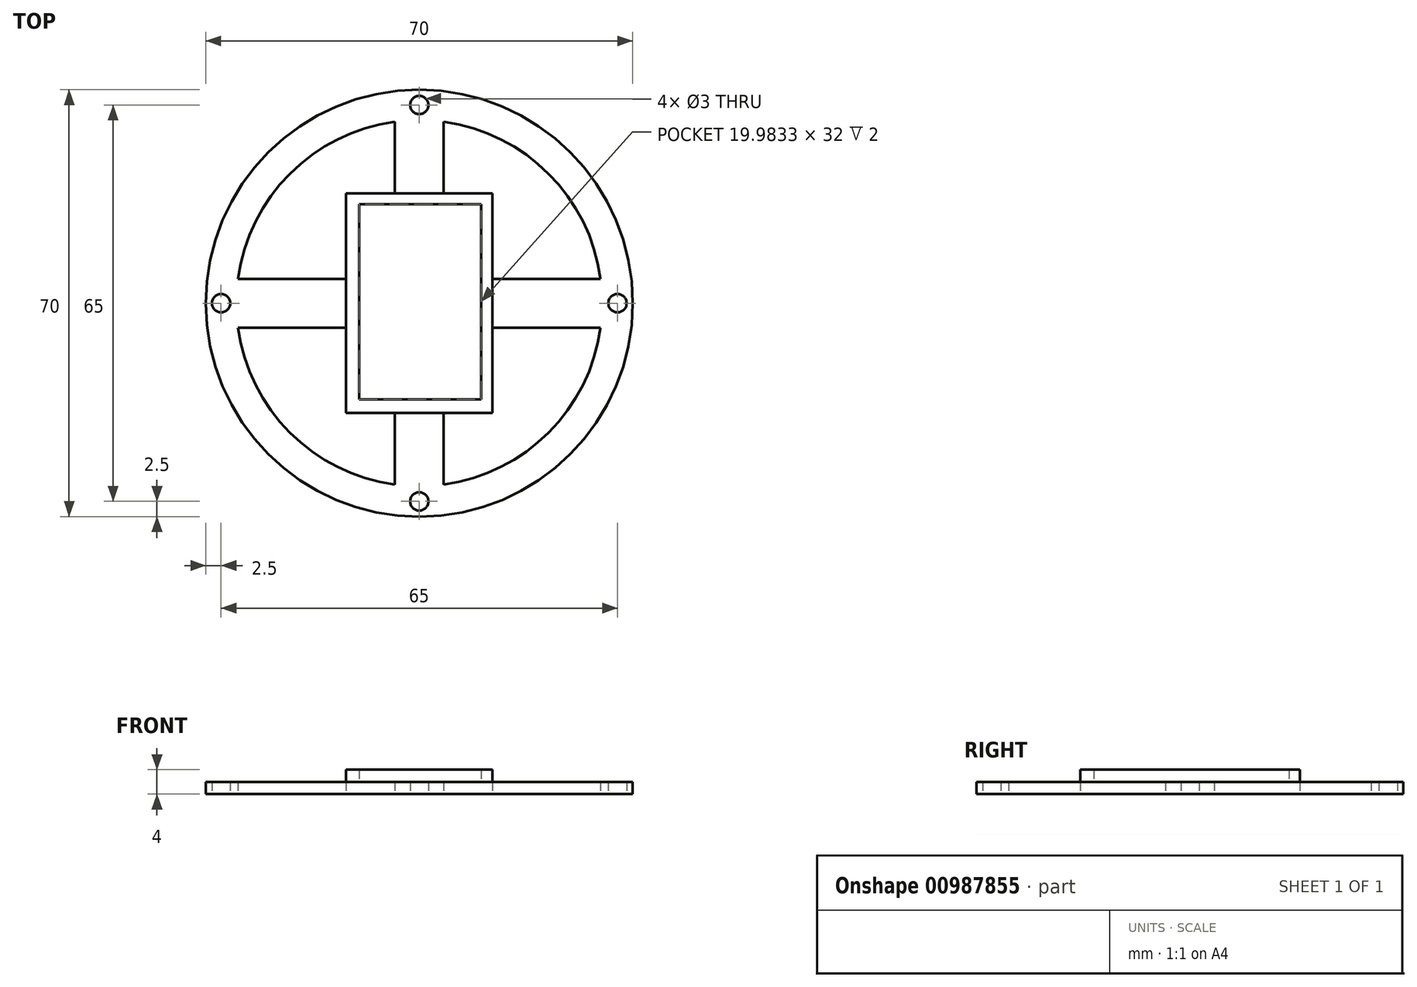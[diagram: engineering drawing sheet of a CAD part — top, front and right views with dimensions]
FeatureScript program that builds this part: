
annotation { "Feature Type Name" : "Feature", "Feature Type Description" : "" }
export const myFeature = defineFeature(function(context is Context, id is Id, definition is map)
    precondition{}
    {
        {
            var Q0;
            Q0=qCreatedBy(makeId("Top.planeOp"),FACE);
            var sketch = newSketch(context, id + "F0", { "sketchPlane" : qUnion([Q0])});
            skCircle(sketch, "E0", {"center": v(0, 0) * mm, "radius": 35 * mm});
            skCircle(sketch, "E1", {"center": v(0, 0) * mm, "radius": 30 * mm});
            skLineSegment(sketch, "E2", {"start": v(-9.84, 16.24) * mm, "end": v(-9.84, -15.76) * mm});
            skLineSegment(sketch, "E3", {"start": v(-9.84, -15.76) * mm, "end": v(10.14, -15.76) * mm});
            skLineSegment(sketch, "E4", {"start": v(10.14, -15.76) * mm, "end": v(10.14, 16.24) * mm});
            skLineSegment(sketch, "E5", {"start": v(10.14, 16.24) * mm, "end": v(-9.86, 16.24) * mm});
            skLineSegment(sketch, "E6", {"start": v(-12, 18) * mm, "end": v(-12, -18) * mm});
            skLineSegment(sketch, "E7", {"start": v(-12, 18) * mm, "end": v(12, 18) * mm});
            skLineSegment(sketch, "E8", {"start": v(12, 18) * mm, "end": v(12, -18) * mm});
            skLineSegment(sketch, "E9", {"start": v(12, -18) * mm, "end": v(-12, -18) * mm});
            skLineSegment(sketch, "E10", {"start": v(-12, 4) * mm, "end": v(-12, 18) * mm});
            skLineSegment(sketch, "E11", {"start": v(12, 12.1) * mm, "end": v(12, -18) * mm});
            skLineSegment(sketch, "E12", {"start": v(4, -18) * mm, "end": v(12, -18) * mm});
            skLineSegment(sketch, "E13", {"start": v(-4, 29.73) * mm, "end": v(-4, 18) * mm});
            skLineSegment(sketch, "E14", {"start": v(-4, 18) * mm, "end": v(-12, 18) * mm});
            skLineSegment(sketch, "E15", {"start": v(-12, -18) * mm, "end": v(-4, -18) * mm});
            skLineSegment(sketch, "E16", {"start": v(-4, -18) * mm, "end": v(-4, -29.73) * mm});
            skLineSegment(sketch, "E17", {"start": v(4, -29.73) * mm, "end": v(4, -18) * mm});
            skLineSegment(sketch, "E18", {"start": v(12, -18) * mm, "end": v(12, 18) * mm});
            skLineSegment(sketch, "E19", {"start": v(4, 18) * mm, "end": v(4, 29.73) * mm});
            skLineSegment(sketch, "E20", {"start": v(-29.73, 4) * mm, "end": v(-12, 4) * mm});
            skLineSegment(sketch, "E21", {"start": v(12, -5.15) * mm, "end": v(12, -18) * mm});
            skLineSegment(sketch, "E22", {"start": v(-12, -18) * mm, "end": v(-12, -4) * mm});
            skLineSegment(sketch, "E23", {"start": v(-12, -4) * mm, "end": v(-29.73, -4) * mm});
            skCircle(sketch, "E24", {"center": v(0, 32.5) * mm, "radius": 1.5 * mm});
            skCircle(sketch, "E25", {"center": v(-32.5, 0) * mm, "radius": 1.5 * mm});
            skCircle(sketch, "E26", {"center": v(32.5, 0) * mm, "radius": 1.5 * mm});
            skCircle(sketch, "E27", {"center": v(0, -32.5) * mm, "radius": 1.5 * mm});
            skLineSegment(sketch, "E28", {"start": v(-28.44, 4) * mm, "end": v(-28.44, 0) * mm, "construction": true});
            skLineSegment(sketch, "E29", {"start": v(-28.44, 0) * mm, "end": v(-28.44, -4) * mm, "construction": true});
            skLineSegment(sketch, "E30.MirrorCS", {"start": v(29.73, 4) * mm, "end": v(12, 4) * mm});
            skLineSegment(sketch, "E31.MirrorCS", {"start": v(12, -4) * mm, "end": v(29.73, -4) * mm});
            skLineSegment(sketch, "E32", {"start": v(-4, 33.6) * mm, "end": v(0, 33.6) * mm, "construction": true});
            skLineSegment(sketch, "E33", {"start": v(0, 33.6) * mm, "end": v(4, 33.6) * mm, "construction": true});
            skLineSegment(sketch, "E34", {"start": v(-32.5, 0) * mm, "end": v(0, 0) * mm, "construction": true});
            skLineSegment(sketch, "E35", {"start": v(0, 0) * mm, "end": v(32.5, 0) * mm, "construction": true});
            skLineSegment(sketch, "E36", {"start": v(0, 0) * mm, "end": v(0, -32.5) * mm, "construction": true});
            skLineSegment(sketch, "E37", {"start": v(0, 32.5) * mm, "end": v(0, 0) * mm, "construction": true});
            skSolve(sketch);
        }
        {
            var Q0;
            Q0=makeQuery(id+"F0.imprint","IMPRINT",FACE,{"disambiguationData":[TD([[makeQuery(id+"F0.imprint","IMPRINT",EDGE,{"derivedFrom":sQuery(id+"F0.wireOp",EDGE,"E0")}),1.0]])]});
            var Q1;
            {var subQ0=sQuery(id+"F0.wireOp",EDGE,"E13");Q1=makeQuery(id+"F0.imprint","IMPRINT",FACE,{"disambiguationData":[TD([[makeQuery(id+"F0.imprint","IMPRINT",EDGE,{"derivedFrom":subQ0}),1.0]])]});}
            var Q2;
            Q2=makeQuery(id+"F0.imprint","IMPRINT",FACE,{"disambiguationData":[TD([[makeQuery(id+"F0.imprint","IMPRINT",EDGE,{"derivedFrom":sQuery(id+"F0.wireOp",EDGE,"E6")}),-1.0]])]});
            var Q3;
            {var subQ0=sQuery(id+"F0.wireOp",EDGE,"ZGUPFVcQ-Tey6-lDge-y4ng-aYvP5VUUE1ul");Q3=makeQuery(id+"F0.imprint","IMPRINT",FACE,{"disambiguationData":[TD([[makeQuery(id+"F0.imprint","IMPRINT",EDGE,{"derivedFrom":subQ0}),-1.0]])]});}
            var Q4;
            Q4=makeQuery(id+"F0.imprint","IMPRINT",FACE,{"disambiguationData":[TD([[makeQuery(id+"F0.imprint","IMPRINT",EDGE,{"derivedFrom":sQuery(id+"F0.wireOp",EDGE,"E9")}),1.0]])]});
            var Q5;
            {var subQ3=sQuery(id+"F0.wireOp",EDGE,"E2");Q5=makeQuery(id+"F0.imprint","IMPRINT",FACE,{"disambiguationData":[TD([[makeQuery(id+"F0.imprint","IMPRINT",EDGE,{"derivedFrom":subQ3}),-1.0]])]});}
            var Q6;
            {var subQ0=sQuery(id+"F0.wireOp",EDGE,"E2");Q6=makeQuery(id+"F0.imprint","IMPRINT",FACE,{"disambiguationData":[TD([[makeQuery(id+"F0.imprint","IMPRINT",EDGE,{"derivedFrom":subQ0}),1.0]])]});}
            var Q7;
            {var subQ2=sQuery(id+"F0.wireOp",EDGE,"OV2fNkNx-53DJ-fSKS-1mRz-XQc7H1Hk84CO");Q7=makeQuery(id+"F0.imprint","IMPRINT",FACE,{"disambiguationData":[TD([[makeQuery(id+"F0.imprint","IMPRINT",EDGE,{"derivedFrom":subQ2}),-1.0]])]});}
            var Q8;
            {var subQ0=sQuery(id+"F0.wireOp",EDGE,"E30.MirrorCS");Q8=makeQuery(id+"F0.imprint","IMPRINT",FACE,{"disambiguationData":[TD([[makeQuery(id+"F0.imprint","IMPRINT",EDGE,{"derivedFrom":subQ0}),1.0]])]});}
            extrude(context, id + "F1", {"entities" : qUnion([Q0, Q1, Q2, Q3, Q4, Q5, Q6, Q7, Q8]), "depth" : 2 * mm, "offsetDistance" : 25 * mm});
        }
        {
            var Q0;
            {var subQ3=sQuery(id+"F0.wireOp",EDGE,"E2");Q0=makeQuery(id+"F0.imprint","IMPRINT",FACE,{"disambiguationData":[TD([[makeQuery(id+"F0.imprint","IMPRINT",EDGE,{"derivedFrom":subQ3}),-1.0]])]});}
            extrude(context, id + "F2", {"entities" : qUnion([Q0]), "operationType" : NewBodyOperationType.ADD, "depth" : 4 * mm, "offsetDistance" : 25 * mm});
        }
    });
